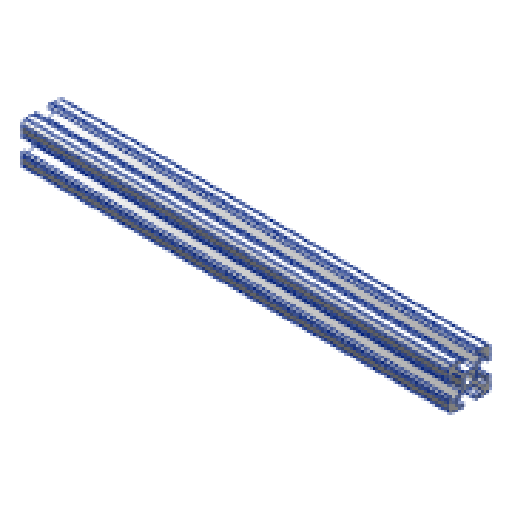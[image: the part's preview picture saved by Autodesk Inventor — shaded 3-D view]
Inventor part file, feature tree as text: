
AUTODESK INVENTOR PART (.ipt)
format: ipt  version: 2025 (Build 290162000, 162)  size: 220,160 bytes
history: native  units: in
note: dims shown in document units (in); Inventor stores cm internally (conversion verified against a paired STEP export)
features: extrude x1, sketch x1
ambient origin geometry x8: Origin, YZ Plane, XZ Plane, XY Plane, X Axis, Y Axis, Z Axis, Center Point
bodies: Solid1 (feature_tree)
feature tree (2):
  extrude  "Extrusion1"  [1 undecoded]
  sketch  "Sketch1"  dims[d0=10.0394in d1=0.0in]
note: 1 required parameter value undecoded (feature->parameter linkage not recoverable at this tier; creation-order binding heuristic only, values carry confidence <= 0.55)
